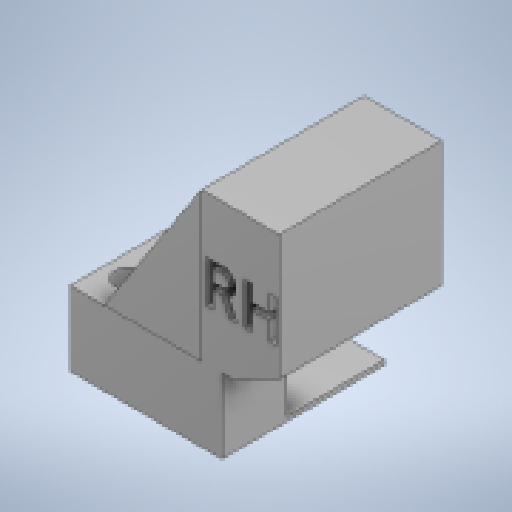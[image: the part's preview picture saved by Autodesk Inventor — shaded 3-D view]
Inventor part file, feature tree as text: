
AUTODESK INVENTOR PART (.ipt)
format: ipt  version: 2024.2 (Build 282272000, 272)  size: 431,616 bytes
history: native  units: in
note: dims shown in document units (in); Inventor stores cm internally (conversion verified against a paired STEP export)
features: sketch x13, extrude x12, projected_geometry x10, other x2, plane x1, mirror x1, hole x1, reference x1
ambient origin geometry x8: Origin, YZ Plane, XZ Plane, XY Plane, X Axis, Y Axis, Z Axis, Center Point
bodies: Solid1 (feature_tree)
feature tree (41):
  extrude  "Extrusion1"  Depth=1.2598in
  plane  "Work Plane1"
  extrude  "Extrusion2"  Depth=0.6299in
  mirror  "Mirror1"
  extrude  "Extrusion3"  TaperAngle=180.0deg  [1 undecoded]
  hole  "Hole1"  [1 undecoded]
  extrude  "Extrusion4"  Depth=0.3543in
  extrude  "Extrusion5"  Depth=1.9685in
  extrude  "Extrusion7"  Depth=0.5906in
  extrude  "Extrusion8"  Depth=1.063in TaperAngle=0.0deg
  extrude  "Extrusion9"  Depth=0.5906in
  extrude  "Extrusion11"  Depth=0.1181in TaperAngle=0.0deg
  extrude  "Extrusion12"  Depth=0.3937in
  extrude  "Extrusion13"  Depth=0.1969in
  extrude  "Extrusion14"  Depth=0.3937in
  sketch  "Sketch1"  dims[d0=1.2598in d2=0.2835in]
  sketch  "Sketch2"  dims[d5=1.378in d6=0.0in d7=0.6299in]
  projected_geometry  "Projected Loop1"
  sketch  "Sketch3"  dims[d9=0.8268in d10=180.0deg]
  projected_geometry  "Projected Loop2"
  sketch  "Sketch4"  dims[d12=0.1181in d13=0.0in d17=2.2441in]
  sketch  "Sketch5"  dims[d18=1.5354in d19=0.3543in]
  projected_geometry  "Projected Loop3"
  sketch  "Sketch6"  dims[d20=0.3543in d21=1.9685in]
  projected_geometry  "Projected Loop4"
  projected_geometry  "Projected Loop6"
  sketch  "Sketch8"  dims[d24=0.6299in d25=0.0in d26=0.5906in]
  projected_geometry  "Projected Loop7"
  sketch  "Sketch9"  dims[d27=0.7874in]
  projected_geometry  "Projected Loop8"
  sketch  "Sketch10"  dims[d28=0.122in d29=0.2362in d30=0.1575in d31=0.0787in d32=90.0deg d33=0.315in d34=0.8108in d37=1.063in d38=0.0in]
  reference  "Reference1"
  sketch  "Sketch12"  dims[d41=0.2283in d42=0.5906in]
  sketch  "Sketch13"  dims[d43=0.7874in d44=0.1181in d45=0.0in]
  projected_geometry  "Projected Loop10"
  sketch  "Sketch14"  dims[d46=1.1811in d47=0.3937in]
  projected_geometry  "Projected Loop11"
  sketch  "Sketch15"  dims[d48=0.0787in d49=0.1969in d55=0.374in d57=1.063in d58=0.5118in d59=0.7677in d68=0.4724in d69=0.5906in d70=0.1969in d71=0.0in d72=0.4724in d73=0.5906in d74=0.1969in d75=0.0in d76=0.7559in d77=0.2283in d78=0.2283in d79=0.2283in d80=0.3937in d81=0.0in d85=0.122in d86=0.1575in d87=0.0in d88=1.2598in d89=0.4331in d90=1.1811in d91=0.0in d92=0.4331in d93=1.9685in d94=0.1969in d95=0.3937in d96=0.0in d97=0.1102in d98=1.5748in d99=0.0in d50=0.0197in d51=0.0344in d52=0.0197in d53=0.0344in d82=0.0197in d83=0.0344in d84=0.0197in d100=0.0197in d101=0.0344in d102=0.0197in d103=0.0344in]
  projected_geometry  "Projected Loop12"
  other  "3_Gripper.iam"
  other  "lm_guide_cart:1"
note: 2 required parameter values undecoded (feature->parameter linkage not recoverable at this tier; creation-order binding heuristic only, values carry confidence <= 0.55)
